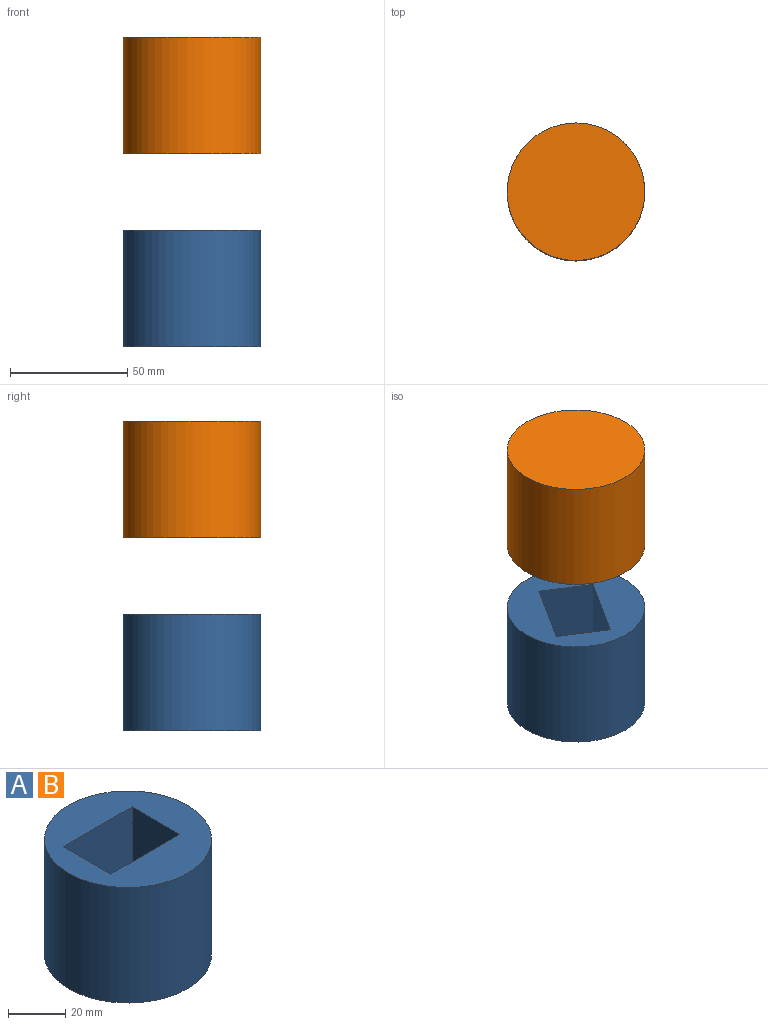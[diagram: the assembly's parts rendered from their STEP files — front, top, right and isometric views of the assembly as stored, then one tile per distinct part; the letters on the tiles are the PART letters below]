
ASSEMBLY  parts=2 mates=2
PART A: 8 faces, bbox 58.6x58.6x49.5 mm
  f0: cylinder r=29.28mm len=58.57mm, axis (0,0,1), area 9113.5mm2, adj f1,f2
  f1: plane 58.57x58.57mm, normal (0,0,-1), area 2694.2mm2, adj f0
  f2: plane 58.57x58.57mm, normal (0,0,1), area 1889.6mm2, adj f0,f3,f4,f5,f6
  f3: plane 35.81x23.58mm, normal (1,0,0), area 844.5mm2, adj f2,f4,f6,f7
  f4: plane 35.81x34.12mm, normal (0,1,0), area 1221.9mm2, adj f2,f3,f5,f7
  f5: plane 35.81x23.58mm, normal (-1,0,0), area 844.5mm2, adj f2,f4,f6,f7
  f6: plane 35.81x34.12mm, normal (0,-1,0), area 1221.9mm2, adj f2,f3,f5,f7
  f7: plane 34.12x23.58mm, normal (0,0,1), area 804.5mm2, adj f3,f4,f5,f6
PART B: same geometry as A
PLACE A rot(axis=(0,0,1),57.5deg) t=(57.49,75.18,-3.07)mm fixed
PLACE B rot(axis=(0.48,-0.88,0),180deg) t=(24,22.66,29.53)mm
MATE cylindrical B.f0 <-> A.f0  axis (0,0,-1) through (23,60.23,54.3)mm
MATE parallel A.f6 <-> B.f6  axis (0.84,-0.54,0) through (10.99,65.3,-3.07)mm
